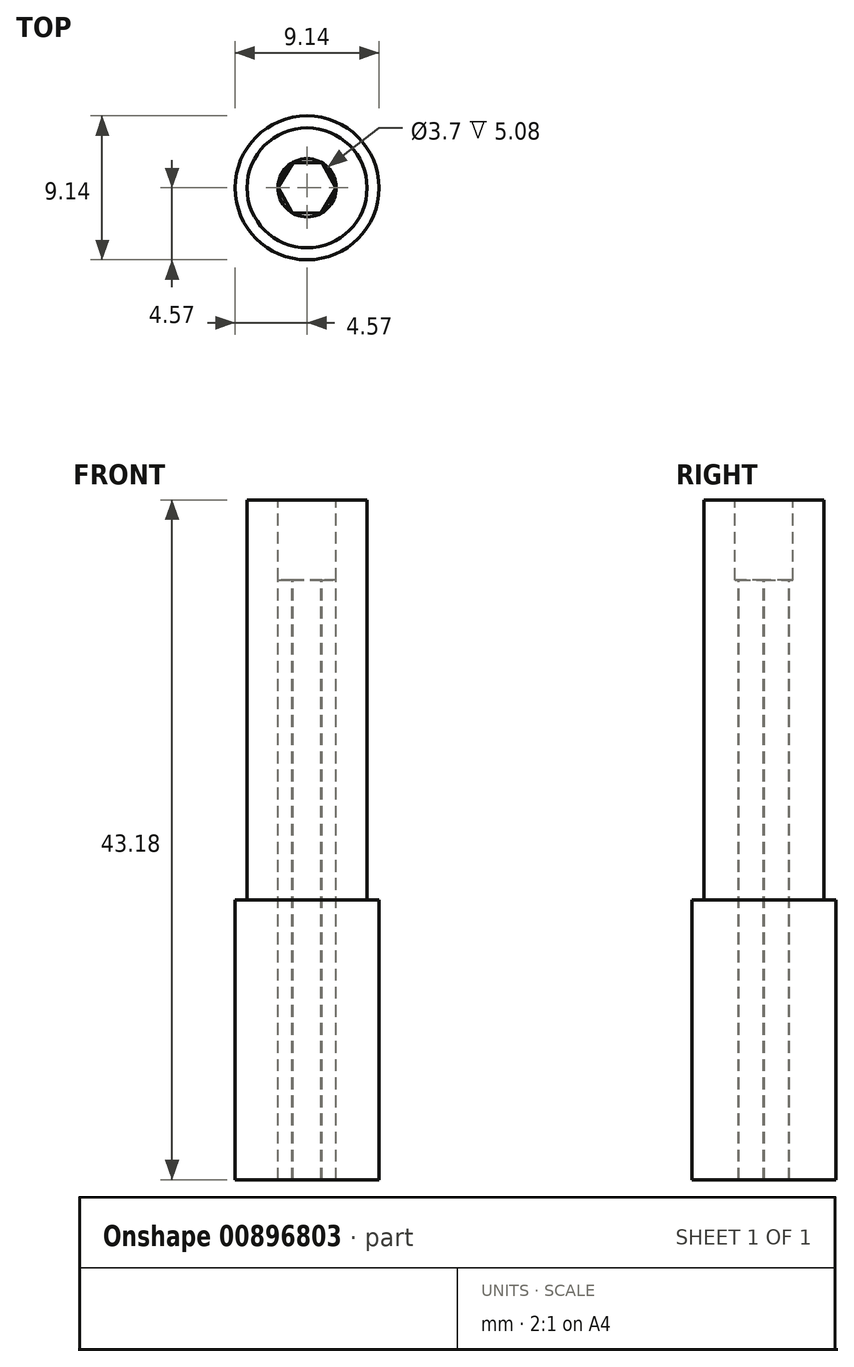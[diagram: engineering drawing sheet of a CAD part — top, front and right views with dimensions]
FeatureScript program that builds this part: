
annotation { "Feature Type Name" : "Feature", "Feature Type Description" : "" }
export const myFeature = defineFeature(function(context is Context, id is Id, definition is map)
    precondition{}
    {
        {
            var Q0;
            Q0=qCreatedBy(makeId("Top.planeOp"),FACE);
            var sketch = newSketch(context, id + "F0", { "sketchPlane" : qUnion([Q0])});
            skCircle(sketch, "E0", {"center": v(0, 0) * mm, "radius": 4.57 * mm});
            skSolve(sketch);
        }
        {
            var Q0;
            Q0 = qSketchRegion(id + "F0", true);
            extrude(context, id + "F1", {"entities" : qUnion([Q0]), "depth" : 17.78 * mm, "offsetDistance" : 25.4 * mm});
        }
        {
            var Q0;
            Q0=makeQuery(id+"F1.opExtrude","CAP_FACE",FACE,{"disambiguationData":[OSD([sQuery(id+"F0.wireOp",EDGE,"E0")])],"isStart":false});
            var sketch = newSketch(context, id + "F2", { "sketchPlane" : qUnion([Q0])});
            skCircle(sketch, "E1", {"center": v(0, 0) * mm, "radius": 3.81 * mm});
            skSolve(sketch);
        }
        {
            var Q0;
            Q0 = qSketchRegion(id + "F2", true);
            extrude(context, id + "F3", {"entities" : qUnion([Q0]), "operationType" : NewBodyOperationType.ADD, "depth" : 25.4 * mm, "offsetDistance" : 25.4 * mm});
        }
        {
            var Q0;
            Q0=makeQuery(id+"F3.opExtrude","CAP_FACE",FACE,{"disambiguationData":[OSD([sQuery(id+"F2.wireOp",EDGE,"E1")])],"isStart":false});
            var sketch = newSketch(context, id + "F4", { "sketchPlane" : qUnion([Q0])});
            skCircle(sketch, "E2.cCircle", {"center": v(0, 0) * mm, "radius": 1.6 * mm, "construction": true});
            skLineSegment(sketch, "E2.0", {"start": v(1.85, -0.03) * mm, "end": v(0.9, -1.61) * mm});
            skLineSegment(sketch, "E2.1", {"start": v(0.9, -1.61) * mm, "end": v(-0.95, -1.58) * mm});
            skLineSegment(sketch, "E2.2", {"start": v(-0.95, -1.58) * mm, "end": v(-1.85, 0.03) * mm});
            skLineSegment(sketch, "E2.3", {"start": v(-1.85, 0.03) * mm, "end": v(-0.9, 1.61) * mm});
            skLineSegment(sketch, "E2.4", {"start": v(-0.9, 1.61) * mm, "end": v(0.95, 1.58) * mm});
            skLineSegment(sketch, "E2.5", {"start": v(0.95, 1.58) * mm, "end": v(1.85, -0.03) * mm});
            skPoint(sketch, "E2.0.midPoint", {"position": v(1.37, -0.82) * mm});
            skSolve(sketch);
        }
        {
            var Q0;
            Q0 = qSketchRegion(id + "F4", true);
            extrude(context, id + "F5", {"entities" : qUnion([Q0]), "operationType" : NewBodyOperationType.REMOVE, "endBound" : BoundingType.THROUGH_ALL, "oppositeDirection" : true, "depth" : 25.4 * mm, "offsetDistance" : 25.4 * mm});
        }
        {
            var Q0;
            Q0=makeQuery(id+"F3.opExtrude","CAP_FACE",FACE,{"disambiguationData":[OSD([sQuery(id+"F2.wireOp",EDGE,"E1")])],"isStart":false});
            var sketch = newSketch(context, id + "F6", { "sketchPlane" : qUnion([Q0])});
            skCircle(sketch, "E3", {"center": v(0, 0) * mm, "radius": 1.85 * mm});
            skSolve(sketch);
        }
        {
            var Q0;
            Q0 = qSketchRegion(id + "F6", true);
            extrude(context, id + "F7", {"entities" : qUnion([Q0]), "operationType" : NewBodyOperationType.REMOVE, "oppositeDirection" : true, "depth" : 5.08 * mm, "offsetDistance" : 25.4 * mm});
        }
    });
